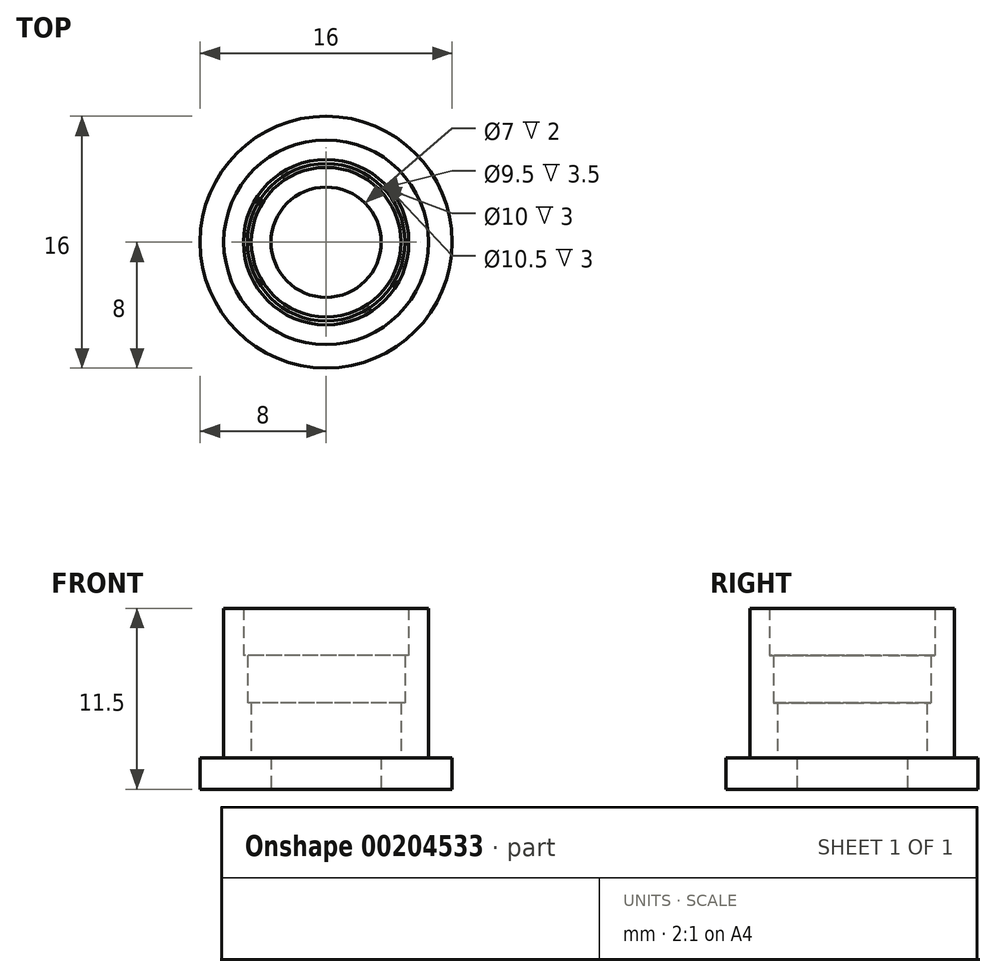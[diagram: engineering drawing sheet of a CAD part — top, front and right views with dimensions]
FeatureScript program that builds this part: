
annotation { "Feature Type Name" : "Feature", "Feature Type Description" : "" }
export const myFeature = defineFeature(function(context is Context, id is Id, definition is map)
    precondition{}
    {
        {
            var Q0;
            Q0=qCreatedBy(makeId("Top.planeOp"),FACE);
            var sketch = newSketch(context, id + "F0", { "sketchPlane" : qUnion([Q0])});
            skCircle(sketch, "E0", {"center": v(0, 0) * mm, "radius": 8 * mm});
            skCircle(sketch, "E1", {"center": v(0, 0) * mm, "radius": 3.5 * mm});
            skSolve(sketch);
        }
        {
            var Q0;
            Q0=makeQuery(id+"F0.imprint","IMPRINT",FACE,{"disambiguationData":[TD([[makeQuery(id+"F0.imprint","IMPRINT",EDGE,{"derivedFrom":sQuery(id+"F0.wireOp",EDGE,"E0")}),1.0]])]});
            extrude(context, id + "F1", {"entities" : qUnion([Q0]), "depth" : 2 * mm});
        }
        {
            var Q0;
            Q0=makeQuery(id+"F1.opExtrude","CAP_FACE",FACE,{"disambiguationData":[OSD([sQuery(id+"F0.wireOp",EDGE,"E0"),sQuery(id+"F0.wireOp",EDGE,"E1")])],"isStart":false});
            var sketch = newSketch(context, id + "F2", { "sketchPlane" : qUnion([Q0])});
            skCircle(sketch, "E2", {"center": v(0, 0) * mm, "radius": 4.75 * mm});
            skCircle(sketch, "E3", {"center": v(0, 0) * mm, "radius": 6.5 * mm});
            skSolve(sketch);
        }
        {
            var Q0;
            Q0=makeQuery(id+"F2.imprint","IMPRINT",FACE,{"disambiguationData":[TD([[makeQuery(id+"F2.imprint","IMPRINT",EDGE,{"derivedFrom":sQuery(id+"F2.wireOp",EDGE,"E2")}),-1.0]])]});
            extrude(context, id + "F3", {"entities" : qUnion([Q0]), "operationType" : NewBodyOperationType.ADD, "depth" : 3.5 * mm});
        }
        {
            var Q0;
            Q0=makeQuery(id+"F3.opExtrude","CAP_FACE",FACE,{"disambiguationData":[OSD([sQuery(id+"F2.wireOp",EDGE,"E2"),sQuery(id+"F2.wireOp",EDGE,"E3")])],"isStart":false});
            var sketch = newSketch(context, id + "F4", { "sketchPlane" : qUnion([Q0])});
            skCircle(sketch, "E4", {"center": v(0, 0) * mm, "radius": 5 * mm});
            skCircle(sketch, "E5", {"center": v(0, 0) * mm, "radius": 6.5 * mm});
            skSolve(sketch);
        }
        {
            var Q0;
            Q0=makeQuery(id+"F4.imprint","IMPRINT",FACE,{"disambiguationData":[TD([[makeQuery(id+"F4.imprint","IMPRINT",EDGE,{"derivedFrom":sQuery(id+"F4.wireOp",EDGE,"E4")}),-1.0]])]});
            extrude(context, id + "F5", {"entities" : qUnion([Q0]), "operationType" : NewBodyOperationType.ADD, "depth" : 3 * mm});
        }
        {
            var Q0;
            Q0=makeQuery(id+"F5.opExtrude","CAP_FACE",FACE,{"disambiguationData":[OSD([sQuery(id+"F4.wireOp",EDGE,"E4"),sQuery(id+"F4.wireOp",EDGE,"E5")])],"isStart":false});
            var sketch = newSketch(context, id + "F6", { "sketchPlane" : qUnion([Q0])});
            skCircle(sketch, "E6", {"center": v(0, 0) * mm, "radius": 5.25 * mm});
            skCircle(sketch, "E7", {"center": v(0, 0) * mm, "radius": 6.5 * mm});
            skSolve(sketch);
        }
        {
            var Q0;
            Q0=makeQuery(id+"F6.imprint","IMPRINT",FACE,{"disambiguationData":[TD([[makeQuery(id+"F6.imprint","IMPRINT",EDGE,{"derivedFrom":sQuery(id+"F6.wireOp",EDGE,"E6")}),-1.0]])]});
            extrude(context, id + "F7", {"entities" : qUnion([Q0]), "operationType" : NewBodyOperationType.ADD, "depth" : 3 * mm});
        }
    });
